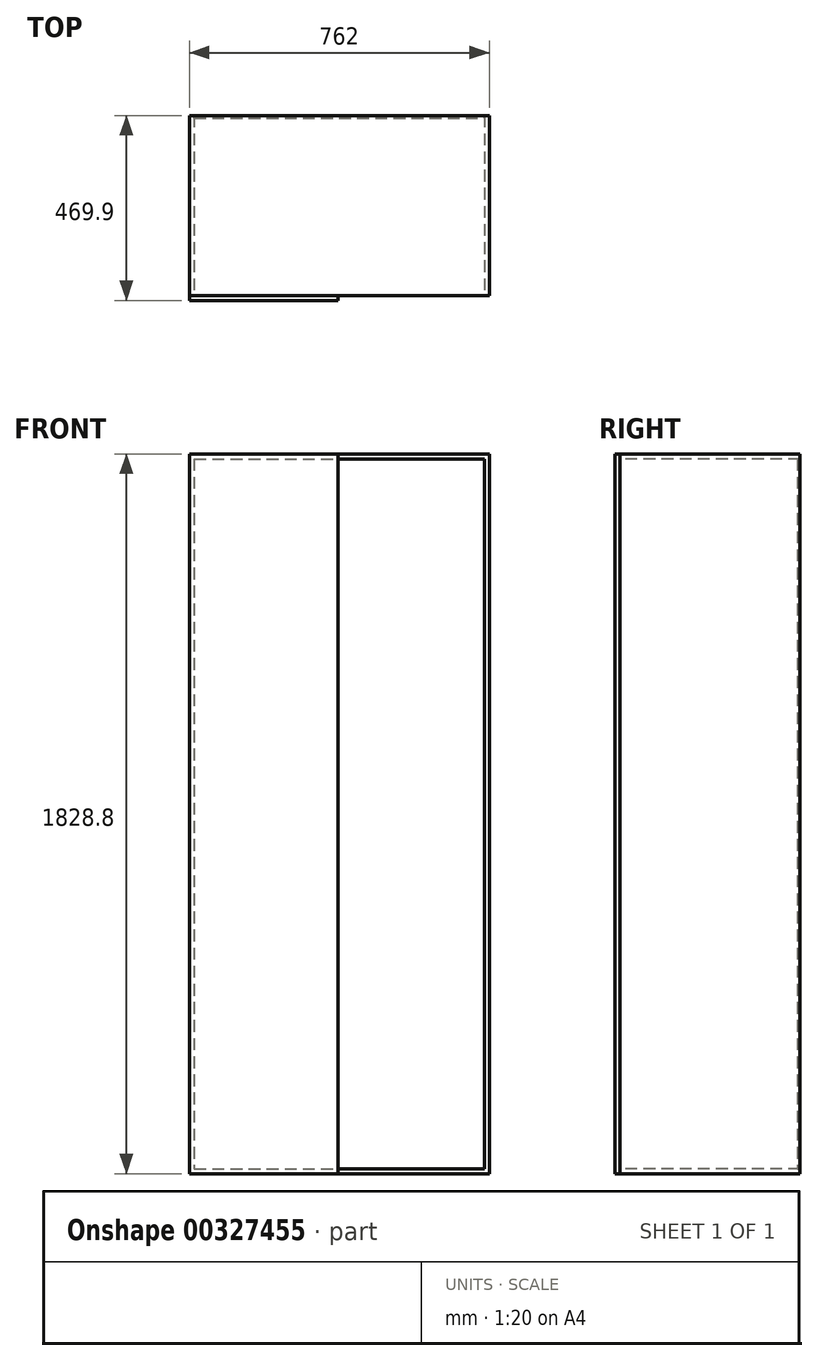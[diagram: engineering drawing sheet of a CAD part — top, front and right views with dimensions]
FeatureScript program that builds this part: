
annotation { "Feature Type Name" : "Feature", "Feature Type Description" : "" }
export const myFeature = defineFeature(function(context is Context, id is Id, definition is map)
    precondition{}
    {
        {
            var Q0;
            Q0=qCreatedBy(makeId("Front.planeOp"),FACE);
            var sketch = newSketch(context, id + "F0", { "sketchPlane" : qUnion([Q0])});
            skLineSegment(sketch, "E0.bottom", {"start": v(-381, 1828.8) * mm, "end": v(381, 1828.8) * mm});
            skLineSegment(sketch, "E0.top", {"start": v(-381, 0) * mm, "end": v(381, 0) * mm});
            skLineSegment(sketch, "E0.left", {"start": v(-381, 1828.8) * mm, "end": v(-381, 0) * mm});
            skLineSegment(sketch, "E0.right", {"start": v(381, 1828.8) * mm, "end": v(381, 0) * mm});
            skLineSegment(sketch, "E1.0", {"start": v(-368.3, 1816.1) * mm, "end": v(-368.3, 12.7) * mm});
            skLineSegment(sketch, "E1.1", {"start": v(-368.3, 1816.1) * mm, "end": v(368.3, 1816.1) * mm});
            skLineSegment(sketch, "E1.2", {"start": v(368.3, 1816.1) * mm, "end": v(368.3, 12.7) * mm});
            skLineSegment(sketch, "E1.3", {"start": v(-368.3, 12.7) * mm, "end": v(368.3, 12.7) * mm});
            skSolve(sketch);
        }
        {
            var Q0;
            Q0=makeQuery(id+"F0.imprint","IMPRINT",FACE,{"disambiguationData":[TD([[makeQuery(id+"F0.imprint","IMPRINT",EDGE,{"derivedFrom":sQuery(id+"F0.wireOp",EDGE,"E0.bottom")}),-1.0]])]});
            extrude(context, id + "F1", {"entities" : qUnion([Q0]), "oppositeDirection" : true, "depth" : 457.2 * mm});
        }
        {
            var Q0;
            Q0=makeQuery(id+"F1.opExtrude","CAP_FACE",FACE,{"disambiguationData":[OSD([sQuery(id+"F0.wireOp",EDGE,"E0.bottom"),sQuery(id+"F0.wireOp",EDGE,"E0.top"),sQuery(id+"F0.wireOp",EDGE,"E0.left"),sQuery(id+"F0.wireOp",EDGE,"E0.right"),sQuery(id+"F0.wireOp",EDGE,"E1.0"),sQuery(id+"F0.wireOp",EDGE,"E1.1"),sQuery(id+"F0.wireOp",EDGE,"E1.2"),sQuery(id+"F0.wireOp",EDGE,"E1.3")])],"isStart":false});
            var sketch = newSketch(context, id + "F2", { "sketchPlane" : qUnion([Q0])});
            skLineSegment(sketch, "E2.bottom", {"start": v(-368.3, 1816.1) * mm, "end": v(368.3, 1816.1) * mm});
            skLineSegment(sketch, "E2.top", {"start": v(-368.3, 12.7) * mm, "end": v(368.3, 12.7) * mm});
            skLineSegment(sketch, "E2.left", {"start": v(-368.3, 1816.1) * mm, "end": v(-368.3, 12.7) * mm});
            skLineSegment(sketch, "E2.right", {"start": v(368.3, 1816.1) * mm, "end": v(368.3, 12.7) * mm});
            skSolve(sketch);
        }
        {
            var Q0;
            Q0=makeQuery(id+"F2.imprint","IMPRINT",FACE,{"disambiguationData":[TD([[makeQuery(id+"F2.imprint","IMPRINT",EDGE,{"derivedFrom":sQuery(id+"F2.wireOp",EDGE,"E2.bottom")}),1.0]])]});
            extrude(context, id + "F3", {"entities" : qUnion([Q0]), "oppositeDirection" : true, "depth" : 6.35 * mm});
        }
        {
            var Q0;
            Q0=makeQuery(id+"F1.opExtrude","CAP_FACE",FACE,{"disambiguationData":[OSD([sQuery(id+"F0.wireOp",EDGE,"E0.bottom"),sQuery(id+"F0.wireOp",EDGE,"E0.top"),sQuery(id+"F0.wireOp",EDGE,"E0.left"),sQuery(id+"F0.wireOp",EDGE,"E0.right"),sQuery(id+"F0.wireOp",EDGE,"E1.0"),sQuery(id+"F0.wireOp",EDGE,"E1.1"),sQuery(id+"F0.wireOp",EDGE,"E1.2"),sQuery(id+"F0.wireOp",EDGE,"E1.3")])],"isStart":true});
            var sketch = newSketch(context, id + "F4", { "sketchPlane" : qUnion([Q0])});
            skLineSegment(sketch, "E3.bottom", {"start": v(-381, 1828.8) * mm, "end": v(-3.18, 1828.8) * mm});
            skLineSegment(sketch, "E3.top", {"start": v(-381, 0) * mm, "end": v(-3.18, 0) * mm});
            skLineSegment(sketch, "E3.left", {"start": v(-381, 1828.8) * mm, "end": v(-381, 0) * mm});
            skLineSegment(sketch, "E3.right", {"start": v(-3.18, 1828.8) * mm, "end": v(-3.18, 0) * mm});
            skSolve(sketch);
        }
        {
            var Q0;
            Q0 = qSketchRegion(id + "F4", true);
            extrude(context, id + "F5", {"entities" : qUnion([Q0]), "depth" : 12.7 * mm});
        }
    });
